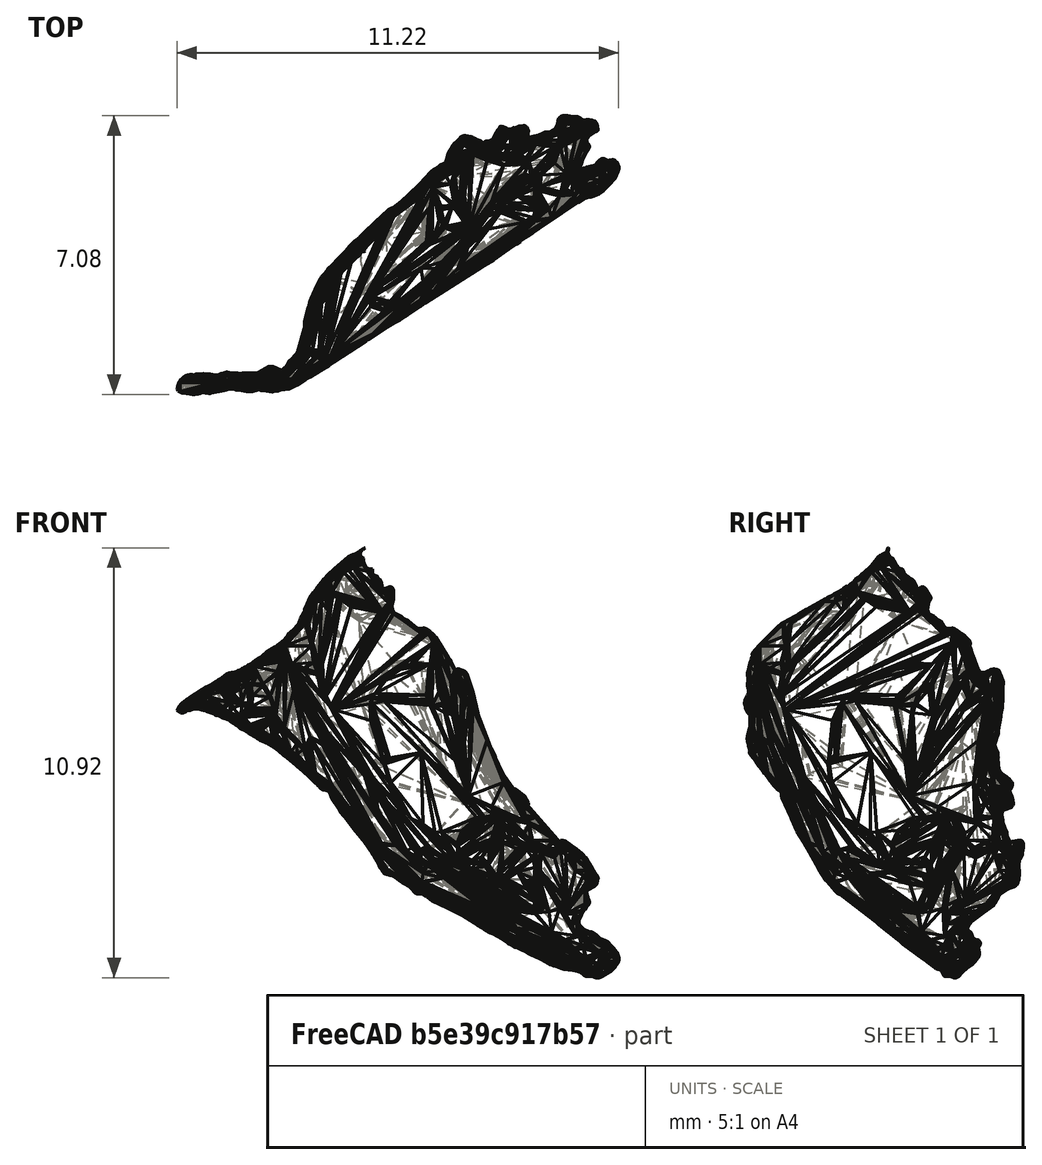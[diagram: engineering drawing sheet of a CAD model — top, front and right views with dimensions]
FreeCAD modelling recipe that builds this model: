
FCSTD DOCUMENT  (FreeCAD 0.20R29603 (Git))
Label: sla
License: All rights reserved
LicenseURL: http://en.wikipedia.org/wiki/All_rights_reserved
objects: Mesh::Feature×2, Part::Feature×1, PartDesign::FeatureBase×1, PartDesign::Point×1, PartDesign::Body×1
note: 4 computed .brp shape members not serialized (recipe doc carries the construction recipe); baked Part::Feature solids carry a one-line shape summary decoded from their .brp

FEATURE [Mesh::Feature] sla
FEATURE [Part::Feature] sla001
  shape: bbox 11.22 x 7.083 x 10.92 mm, 12628 faces, 0 solids (baked)
FEATURE [PartDesign::FeatureBase] BaseFeature
  BaseFeature = -> sla001
FEATURE [Mesh::Feature] i_sclerite
FEATURE [PartDesign::Point] DatumPoint  label="i_sclerite_DatumPoint"
  AttacherType = Attacher::AttachEnginePoint
  AttachmentOffset = pos=(-0.1,1.1,3.8) rot=(0,0,1;0rad)
  MapMode = 32
  Placement = pos=(-0.1,1.1,3.8) rot=(0,0,1;0rad)
  Support = -> [XY_Plane]
FEATURE [PartDesign::Body] Body  label="sla_Body"
  BaseFeature = -> sla001
  Group = -> [BaseFeature,DatumPoint]
  Origin = -> Origin
  Tip = -> BaseFeature
